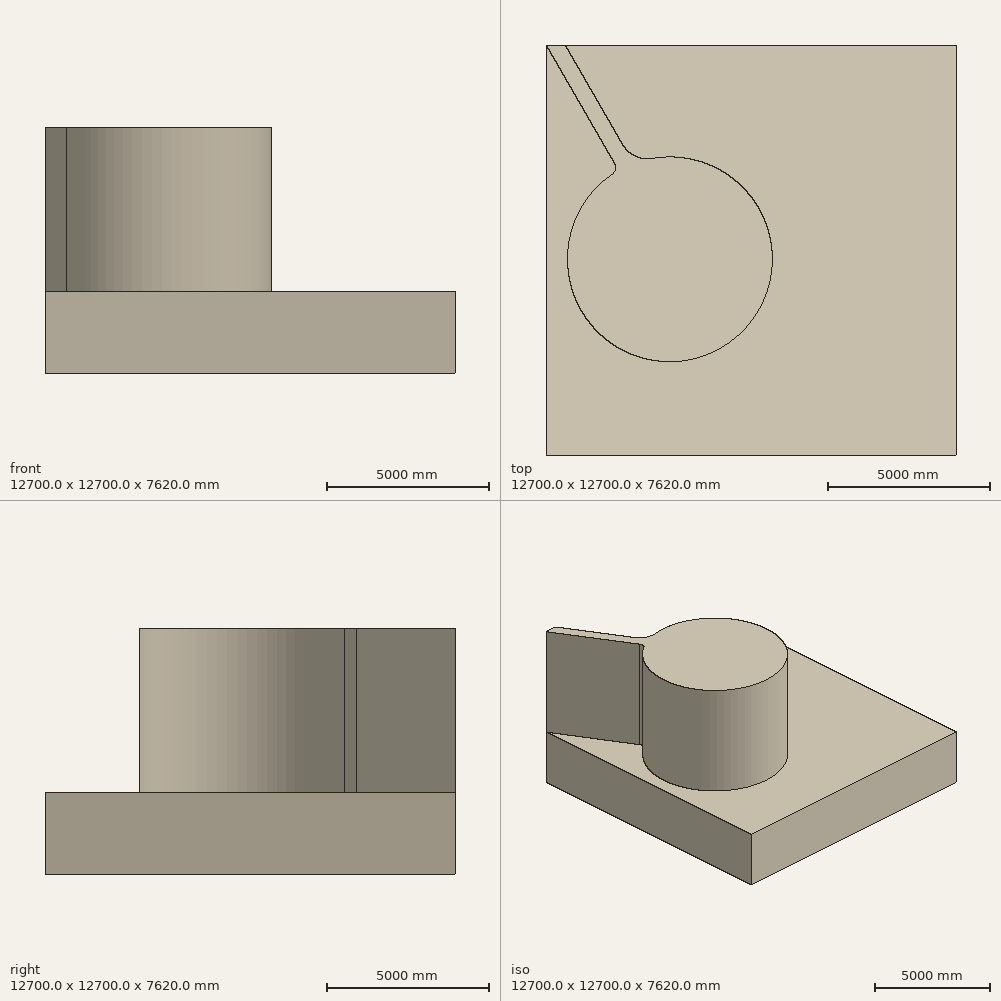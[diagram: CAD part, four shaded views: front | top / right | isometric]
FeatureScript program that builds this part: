
annotation { "Feature Type Name" : "Feature", "Feature Type Description" : "" }
export const myFeature = defineFeature(function(context is Context, id is Id, definition is map)
    precondition{}
    {
        {
            var Q0;
            Q0=qCreatedBy(makeId("Top.planeOp"),FACE);
            var sketch = newSketch(context, id + "F0", { "sketchPlane" : qUnion([Q0])});
            skLineSegment(sketch, "E0.bottom", {"start": v(-12649.47, 12657.89) * mm, "end": v(50.53, 12657.89) * mm});
            skLineSegment(sketch, "E0.top", {"start": v(-12649.47, -42.11) * mm, "end": v(50.53, -42.11) * mm});
            skLineSegment(sketch, "E0.left", {"start": v(-12649.47, 12657.89) * mm, "end": v(-12649.47, -42.11) * mm});
            skLineSegment(sketch, "E0.right", {"start": v(50.53, 12657.89) * mm, "end": v(50.53, -42.11) * mm});
            skSolve(sketch);
        }
        {
            var Q0;
            Q0=makeQuery(id+"F0.imprint","IMPRINT",FACE,{"disambiguationData":[TD([[makeQuery(id+"F0.imprint","IMPRINT",EDGE,{"derivedFrom":sQuery(id+"F0.wireOp",EDGE,"E0.bottom")}),-1.0]])]});
            extrude(context, id + "F1", {"entities" : qUnion([Q0]), "depth" : 2540 * mm});
        }
        {
            var Q0;
            Q0=makeQuery(id+"F1.opExtrude","CAP_FACE",FACE,{"disambiguationData":[OSD([sQuery(id+"F0.wireOp",EDGE,"E0.bottom"),sQuery(id+"F0.wireOp",EDGE,"E0.top"),sQuery(id+"F0.wireOp",EDGE,"E0.left"),sQuery(id+"F0.wireOp",EDGE,"E0.right")])],"isStart":false});
            var sketch = newSketch(context, id + "F2", { "sketchPlane" : qUnion([Q0])});
            skLineSegment(sketch, "E1", {"start": v(-12649.47, 12657.89) * mm, "end": v(-10535.34, 8996.1) * mm});
            skArc(sketch, "E2", {"start": v(-10612.36, 8659.15) * mm, "mid": v(-7632.51, 3092.34) * mm, "end": v(-9371.12, 9162.44) * mm});
            skLineSegment(sketch, "E3.0", {"start": v(-12062.88, 12657.89) * mm, "end": v(-10293.78, 9593.72) * mm});
            skLineSegment(sketch, "E4", {"start": v(-12649.47, 12657.89) * mm, "end": v(-12062.88, 12657.89) * mm});
            skPoint(sketch, "E5.visualSharp", {"position": v(-9952.65, 9002.87) * mm});
            skArc(sketch, "E5.filletArc", {"start": v(-9974.12, 9040.05) * mm, "mid": v(-9947.5, 9017.71) * mm, "end": v(-9912.73, 9017.73) * mm});
            skPoint(sketch, "E6.visualSharp", {"position": v(-10413.05, 8784.3) * mm});
            skArc(sketch, "E6.filletArc", {"start": v(-10612.36, 8659.15) * mm, "mid": v(-10507.7, 8812.5) * mm, "end": v(-10535.34, 8996.1) * mm});
            skArc(sketch, "E7.filletArc", {"start": v(-10293.78, 9593.72) * mm, "mid": v(-9900.33, 9232.85) * mm, "end": v(-9371.12, 9162.44) * mm});
            skSolve(sketch);
        }
        {
            var Q0;
            Q0=makeQuery(id+"F2.imprint","IMPRINT",FACE,{"disambiguationData":[TD([[makeQuery(id+"F2.imprint","IMPRINT",EDGE,{"derivedFrom":sQuery(id+"F2.wireOp",EDGE,"E1")}),1.0]])]});
            extrude(context, id + "F3", {"entities" : qUnion([Q0]), "operationType" : NewBodyOperationType.ADD, "depth" : 5080 * mm});
        }
    });
